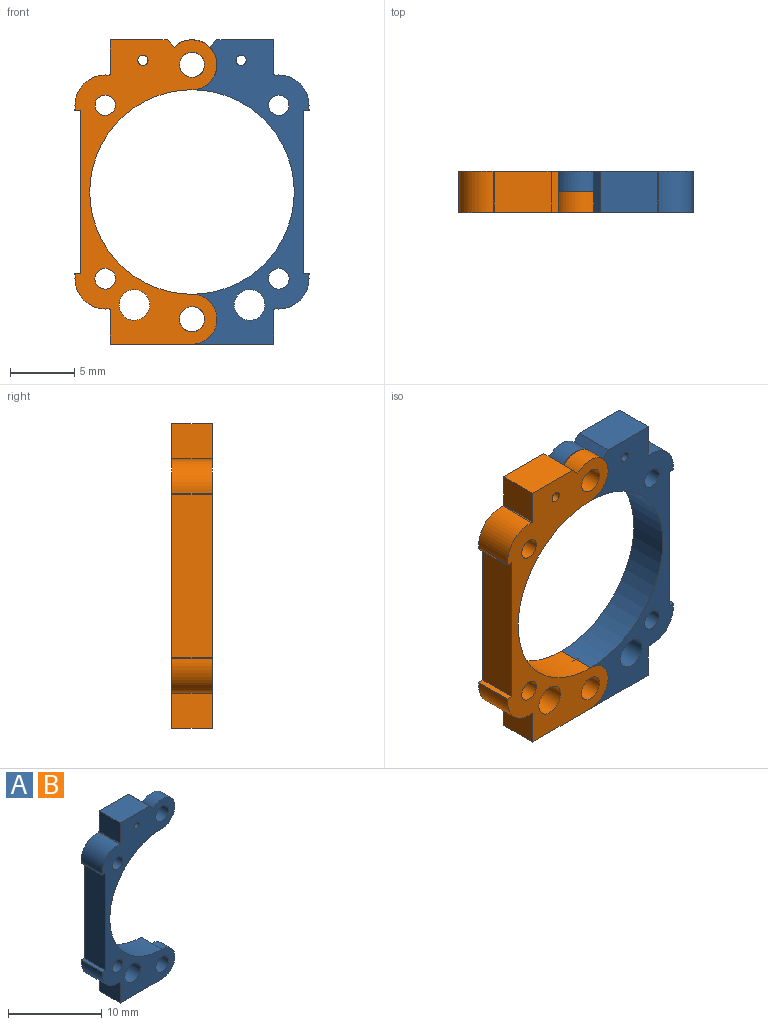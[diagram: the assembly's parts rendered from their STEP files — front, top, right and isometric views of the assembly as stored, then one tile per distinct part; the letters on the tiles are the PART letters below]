
ASSEMBLY  parts=2 mates=1
PART A: 29 faces, bbox 11.1x3.2x23.6 mm
  f0: plane 3.87x3.87mm, normal (0,1,0), area 8.8mm2, adj f19,f22,f26
  f1: plane 3.87x3.87mm, normal (0,1,0), area 8.8mm2, adj f3,f24,f27
  f2: cylinder r=7.94mm len=15.88mm, axis (0,1,0), area 79.2mm2, adj f3,f22,f25,f26,f27,f28
  f3: cylinder r=1.94mm len=3.87mm, axis (0,1,0), area 12.1mm2, adj f1,f2,f4,f25
  f4: plane 3.18x0.57mm, normal (0.71,0,0.71), area 2.5mm2, adj f3,f5,f25,f27,f28
  f5: plane 4.41x3.18mm, normal (0,0,1), area 14mm2, adj f4,f6,f25,f28
  f6: plane 3.18x2.69mm, normal (-1,0,0), area 8.5mm2, adj f5,f7,f25,f28
  f7: cylinder r=11.11mm len=3.18mm, axis (0,1,0), area 0.3mm2, adj f6,f8,f25,f28
  f8: cylinder r=2.35mm len=3.18mm, axis (0,1,0), area 13.7mm2, adj f7,f9,f25,f28
  f9: cylinder r=11.11mm len=3.18mm, axis (0,1,0), area 0.3mm2, adj f8,f10,f25,f28
  f10: plane 3.18x0.48mm, normal (0,0,-1), area 1.5mm2, adj f9,f11,f25,f28
  f11: plane 12.7x3.18mm, normal (-1,0,0), area 40.3mm2, adj f10,f12,f25,f28
  f12: plane 3.18x0.48mm, normal (0,0,1), area 1.5mm2, adj f11,f13,f25,f28
  f13: cylinder r=11.11mm len=3.18mm, axis (0,1,0), area 0.3mm2, adj f12,f14,f25,f28
  f14: cylinder r=2.35mm len=3.18mm, axis (0,1,0), area 13.7mm2, adj f13,f15,f25,f28
  f15: cylinder r=11.11mm len=3.18mm, axis (0,1,0), area 0.3mm2, adj f14,f16,f25,f28
  f16: plane 3.18x2.69mm, normal (-1,0,0), area 8.5mm2, adj f15,f17,f25,f28
  f17: plane 6.35x3.18mm, normal (0,0,-1), area 20.2mm2, adj f16,f22,f25,f26,f28
  f18: cylinder r=0.4mm len=3.18mm, axis (0,1,0), area 7.9mm2, adj f25,f28
  f19: cylinder r=0.98mm len=1.96mm, axis (0,1,0), area 9.8mm2, adj f0,f25
  f20: cylinder r=0.79mm len=3.18mm, axis (0,1,0), area 15.8mm2, adj f25,f28
  f21: cylinder r=0.8mm len=3.18mm, axis (0,1,0), area 16mm2, adj f25,f28
  f22: cylinder r=1.94mm len=3.87mm, axis (0,1,0), area 9.7mm2, adj f0,f2,f17,f25
  f23: cylinder r=1.19mm len=3.18mm, axis (0,1,0), area 23.8mm2, adj f25,f28
  f24: cylinder r=0.97mm len=1.94mm, axis (0,1,0), area 9.7mm2, adj f1,f25
  f25: plane 23.62x11.06mm, normal (0,-1,0), area 89.1mm2, adj f2,f3,f4,f5,f6,f7,f8,f9
  f26: cylinder r=1.94mm len=3.87mm, axis (0,-1,0), area 9.7mm2, adj f0,f2,f17,f28
  f27: cylinder r=1.94mm len=3.31mm, axis (0,-1,0), area 7.2mm2, adj f1,f2,f4,f28
  f28: plane 23.62x9.12mm, normal (0,1,0), area 71.5mm2, adj f2,f4,f5,f6,f7,f8,f9,f10
PART B: same geometry as A
PLACE A rot(axis=(0,0,-1),180deg) t=(-5.07,-0.62,4.82)mm
PLACE B t=(-5.07,-0.62,4.82)mm
MATE revolute A.f3 <-> B.f3  axis (0,-1,0) through (-5.07,-0.62,14.69)mm
